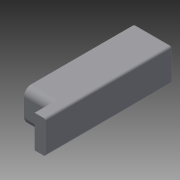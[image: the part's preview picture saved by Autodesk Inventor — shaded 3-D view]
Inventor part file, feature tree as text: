
AUTODESK INVENTOR PART (.ipt)
format: ipt  version: 2015 (Build 190159000, 159)  size: 101,888 bytes
history: native  units: in
note: dims shown in document units (in); Inventor stores cm internally (conversion verified against a paired STEP export)
features: fillet x2, extrude x1, sketch x1
ambient origin geometry x8: Origin, YZ Plane, XZ Plane, XY Plane, X Axis, Y Axis, Z Axis, Center Point
bodies: Solid1 (feature_tree)
feature tree (4):
  extrude  "Extrusion1"  Depth=5.748in
  fillet  "Fillet1"  Radius=1.6732in
  fillet  "Fillet2"  Radius=0.3937in
  sketch  "Sketch1"  dims[d0=2.0079in d1=5.748in d2=1.6732in d3=0.0in d4=0.3937in d5=0.1181in]
